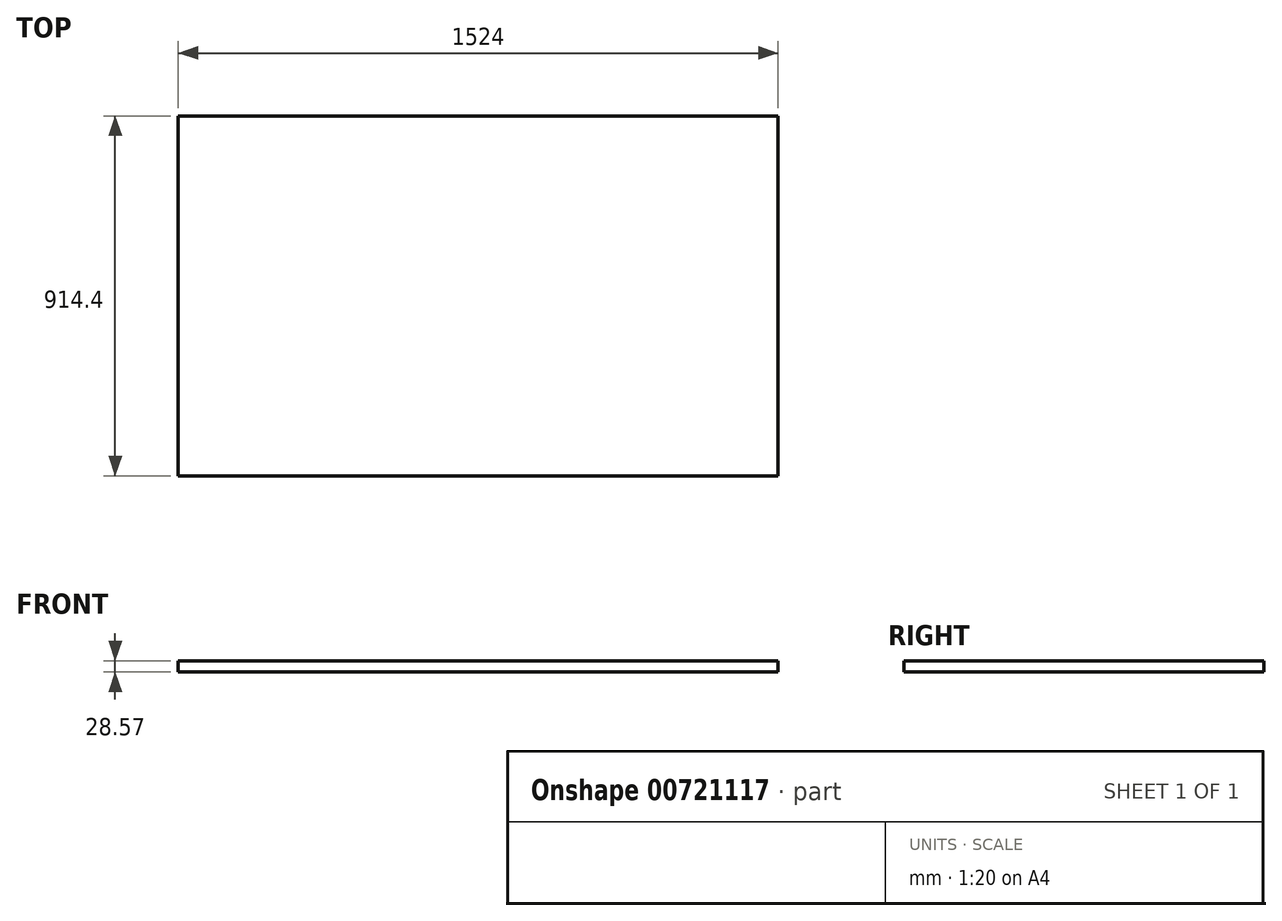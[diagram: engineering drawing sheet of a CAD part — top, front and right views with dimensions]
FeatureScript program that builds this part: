
annotation { "Feature Type Name" : "Feature", "Feature Type Description" : "" }
export const myFeature = defineFeature(function(context is Context, id is Id, definition is map)
    precondition{}
    {
        {
            var Q0;
            Q0=qCreatedBy(makeId("Top.planeOp"),FACE);
            var sketch = newSketch(context, id + "F0", { "sketchPlane" : qUnion([Q0])});
            skLineSegment(sketch, "E0.bottom", {"start": v(762, 457.2) * mm, "end": v(-762, 457.2) * mm});
            skLineSegment(sketch, "E0.top", {"start": v(762, -457.2) * mm, "end": v(-762, -457.2) * mm});
            skLineSegment(sketch, "E0.left", {"start": v(762, 457.2) * mm, "end": v(762, -457.2) * mm});
            skLineSegment(sketch, "E0.right", {"start": v(-762, 457.2) * mm, "end": v(-762, -457.2) * mm});
            skPoint(sketch, "E0.middle", {"position": v(0, 0) * mm});
            skSolve(sketch);
        }
        {
            var Q0;
            Q0=makeQuery(id+"F0.imprint","IMPRINT",FACE,{"disambiguationData":[TD([[makeQuery(id+"F0.imprint","IMPRINT",EDGE,{"derivedFrom":sQuery(id+"F0.wireOp",EDGE,"E0.bottom")}),1.0]])]});
            extrude(context, id + "F1", {"entities" : qUnion([Q0]), "depth" : 28.57 * mm, "offsetDistance" : 25.4 * mm});
        }
    });
